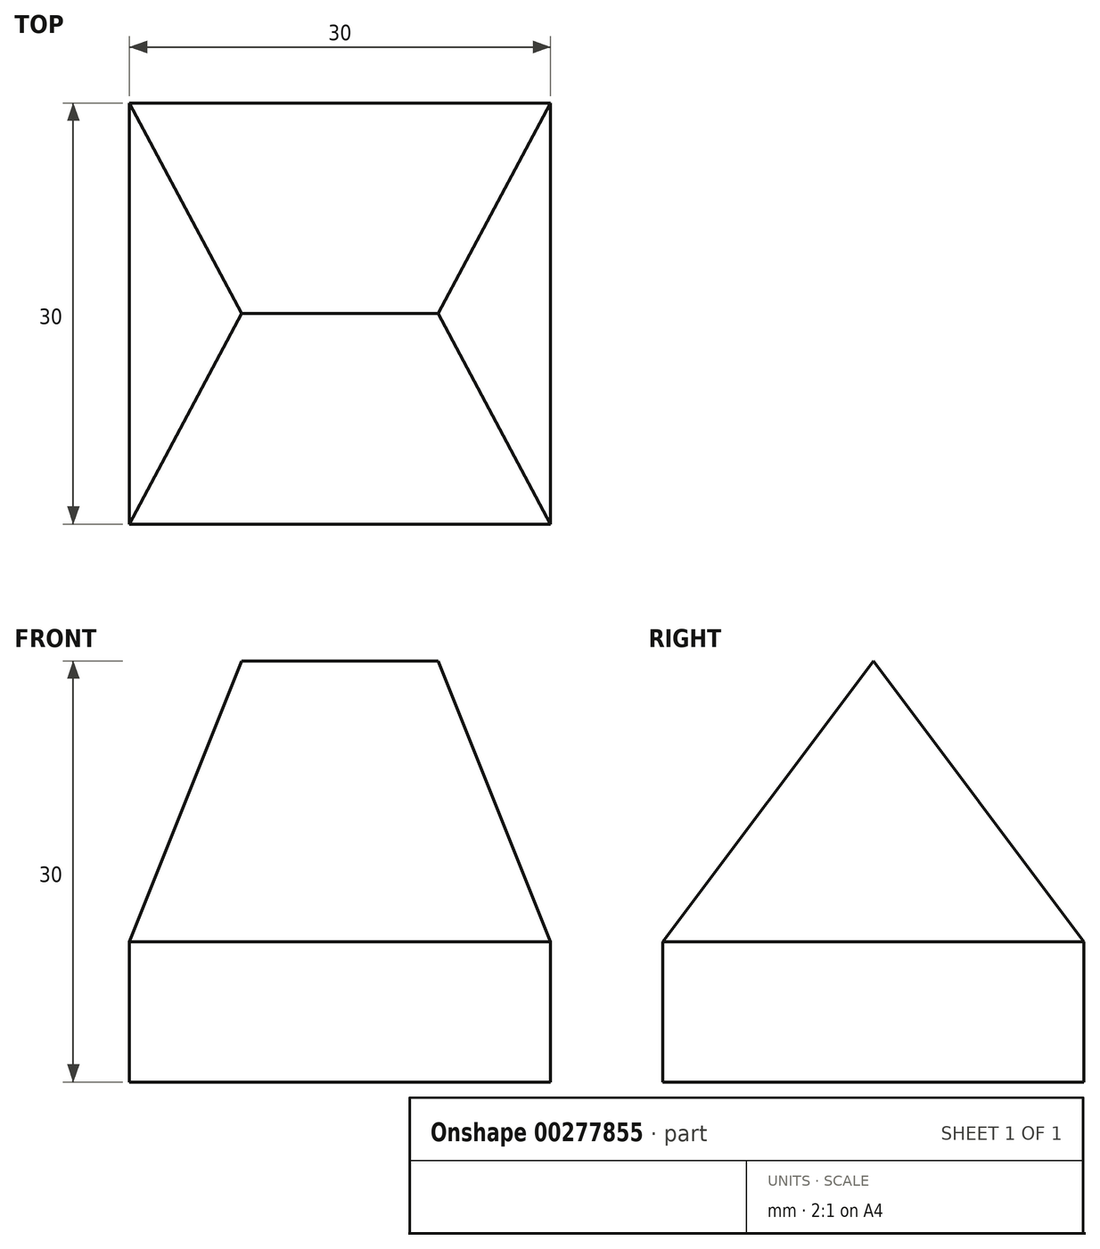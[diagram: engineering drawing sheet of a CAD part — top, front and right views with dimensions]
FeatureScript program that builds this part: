
annotation { "Feature Type Name" : "Feature", "Feature Type Description" : "" }
export const myFeature = defineFeature(function(context is Context, id is Id, definition is map)
    precondition{}
    {
        {
            var Q0;
            Q0=qCreatedBy(makeId("Right.planeOp"),FACE);
            var sketch = newSketch(context, id + "F0", { "sketchPlane" : qUnion([Q0])});
            skLineSegment(sketch, "E0.bottom", {"start": v(0, 0) * mm, "end": v(30, 0) * mm});
            skLineSegment(sketch, "E0.left", {"start": v(0, 0) * mm, "end": v(0, 10) * mm});
            skLineSegment(sketch, "E0.right", {"start": v(30, 0) * mm, "end": v(30, 10) * mm});
            skLineSegment(sketch, "E1", {"start": v(15, 0) * mm, "end": v(15, 37.55) * mm, "construction": true});
            skLineSegment(sketch, "E2", {"start": v(0, 10) * mm, "end": v(15, 30) * mm});
            skLineSegment(sketch, "E3", {"start": v(15, 30) * mm, "end": v(30, 10) * mm});
            skSolve(sketch);
        }
        {
            var Q0;
            Q0 = qSketchRegion(id + "F0", true);
            extrude(context, id + "F1", {"entities" : qUnion([Q0]), "depth" : 30 * mm});
        }
        {
            var Q0;
            Q0=makeQuery(id+"F1.opExtrude","SWEPT_FACE",FACE,{"disambiguationData":[OSD([sQuery(id+"F0.wireOp",EDGE,"E0.left")])]});
            var sketch = newSketch(context, id + "F2", { "sketchPlane" : qUnion([Q0])});
            skLineSegment(sketch, "E4.0", {"start": v(30, 30) * mm, "end": v(22, 30) * mm});
            skLineSegment(sketch, "E5.0", {"start": v(30, 10) * mm, "end": v(30, 30) * mm});
            skLineSegment(sketch, "E5.1", {"start": v(0, 10) * mm, "end": v(0, 30) * mm});
            skLineSegment(sketch, "E6", {"start": v(30, 10) * mm, "end": v(22, 30) * mm});
            skLineSegment(sketch, "E7", {"start": v(0, 10) * mm, "end": v(8, 30) * mm});
            skLineSegment(sketch, "E8.trimOffspring", {"start": v(8, 30) * mm, "end": v(0, 30) * mm});
            skSolve(sketch);
        }
        {
            var Q0;
            Q0 = qSketchRegion(id + "F2", true);
            extrude(context, id + "F3", {"entities" : qUnion([Q0]), "operationType" : NewBodyOperationType.REMOVE, "endBound" : BoundingType.THROUGH_ALL, "oppositeDirection" : true, "depth" : 25 * mm});
        }
    });
